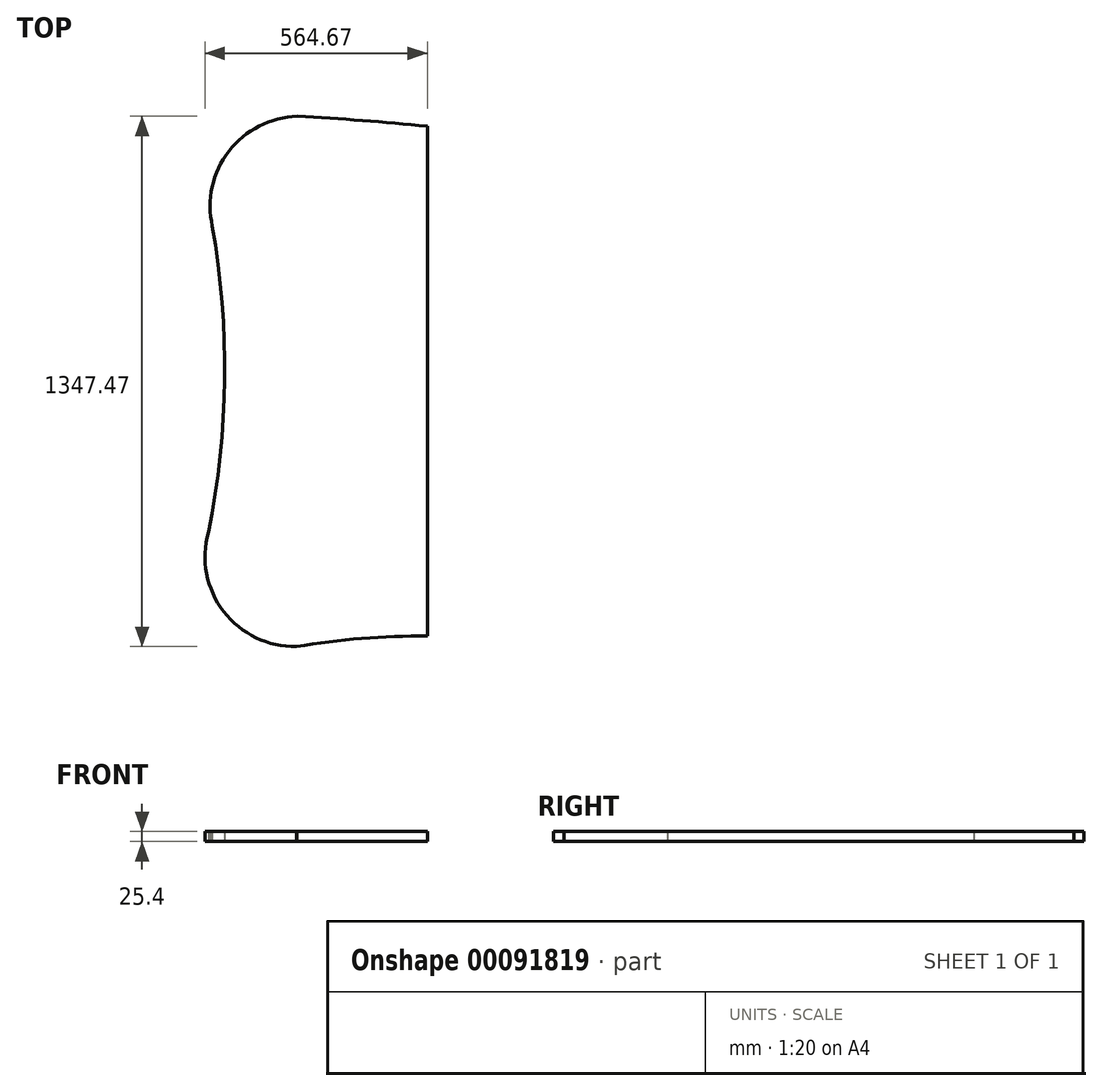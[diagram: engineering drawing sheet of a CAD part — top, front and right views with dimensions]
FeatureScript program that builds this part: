
annotation { "Feature Type Name" : "Feature", "Feature Type Description" : "" }
export const myFeature = defineFeature(function(context is Context, id is Id, definition is map)
    precondition{}
    {
        {
            var Q0;
            Q0=qCreatedBy(makeId("Top.planeOp"),FACE);
            var sketch = newSketch(context, id + "F0", { "sketchPlane" : qUnion([Q0])});
            skLineSegment(sketch, "E0", {"start": v(-122.75, 642.69) * mm, "end": v(-122.75, 388.69) * mm});
            skArc(sketch, "E1", {"start": v(-678.8, -388.6) * mm, "mid": v(-637.61, -0.43) * mm, "end": v(-668.85, 388.69) * mm});
            skArc(sketch, "E2", {"start": v(-452.95, 668.09) * mm, "mid": v(-626.87, 579.37) * mm, "end": v(-668.85, 388.69) * mm});
            skArc(sketch, "E3", {"start": v(-678.8, -388.6) * mm, "mid": v(-639.9, -590.3) * mm, "end": v(-454.8, -679.34) * mm});
            skLineSegment(sketch, "E4", {"start": v(-122.75, 642.69) * mm, "end": v(-122.75, -652.59) * mm});
            skArc(sketch, "E5", {"start": v(-122.75, 642.69) * mm, "mid": v(-287.7, 657.38) * mm, "end": v(-452.95, 668.09) * mm});
            skArc(sketch, "E6", {"start": v(-122.75, -652.59) * mm, "mid": v(-289.37, -658.55) * mm, "end": v(-454.8, -679.34) * mm});
            skSolve(sketch);
        }
        {
            var Q0;
            Q0=makeQuery(id+"F0.imprint","IMPRINT",FACE,{"disambiguationData":[TD([[makeQuery(id+"F0.imprint","IMPRINT",EDGE,{"derivedFrom":sQuery(id+"F0.wireOp",EDGE,"e7358e8d-3bd0-44fc-b618-9dafbb7d24566.MirrorCS")}),1.0]])]});
            var Q1;
            {var subQ0=sQuery(id+"F0.wireOp",EDGE,"E4");var subQ3=makeQuery(id+"F0.imprint","IMPRINT",VERTEX,{"derivedFrom":subQ0});Q1=makeQuery(id+"F0.imprint","IMPRINT",FACE,{"disambiguationData":[TD([[makeQuery(id+"F0.imprint","IMPRINT",EDGE,{"disambiguationData":[TD([[subQ3,1.0]])],"derivedFrom":subQ0}),1.0]])]});}
            var Q2;
            Q2=makeQuery(id+"F0.imprint","IMPRINT",FACE,{"disambiguationData":[TD([[makeQuery(id+"F0.imprint","IMPRINT",EDGE,{"derivedFrom":sQuery(id+"F0.wireOp",EDGE,"E1")}),-1.0]])]});
            extrude(context, id + "F1", {"entities" : qUnion([Q0, Q1, Q2]), "depth" : 25.4 * mm});
        }
    });
